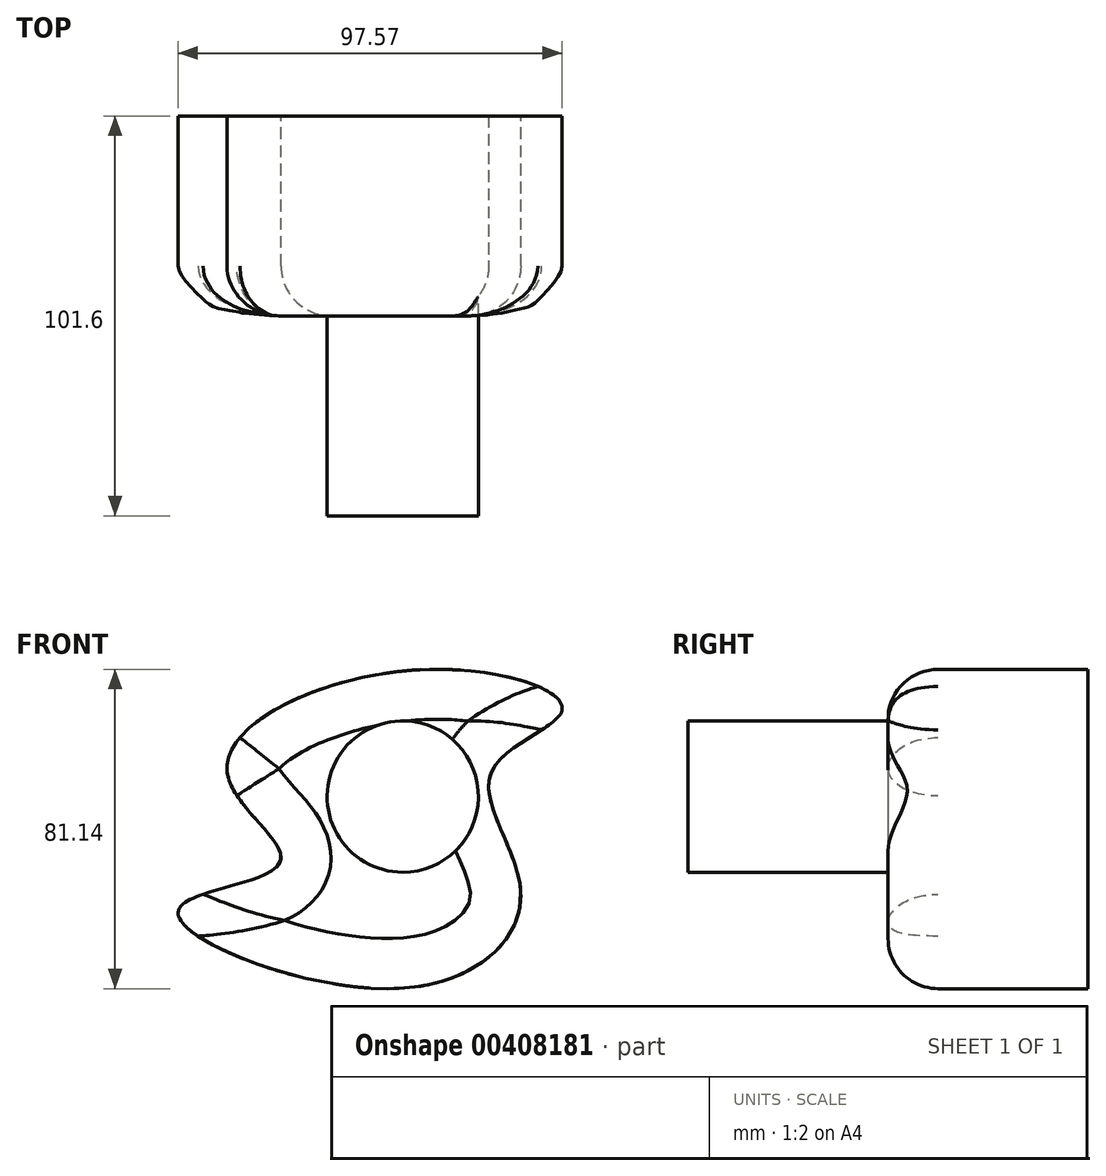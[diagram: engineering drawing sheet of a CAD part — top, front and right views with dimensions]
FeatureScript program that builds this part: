
annotation { "Feature Type Name" : "Feature", "Feature Type Description" : "" }
export const myFeature = defineFeature(function(context is Context, id is Id, definition is map)
    precondition{}
    {
        {
            var Q0;
            Q0=qCreatedBy(makeId("Front.planeOp"),FACE);
            var sketch = newSketch(context, id + "F0", { "sketchPlane" : qUnion([Q0])});
            skFitSpline(sketch, "E0", {"points": [v(39.34, -7.58) * mm, v(31.94, 23.1) * mm, v(49.8, 38.62) * mm, v(11.73, 48.9) * mm, v(-35.19, 22.74) * mm, v(-21.83, 0) * mm, v(-47.46, -11.73) * mm, v(8.3, -31.94) * mm, v(39.34, -7.58) * mm]});
            skSolve(sketch);
        }
        {
            var Q0;
            Q0 = qSketchRegion(id + "F0", true);
            extrude(context, id + "F1", {"entities" : qUnion([Q0]), "depth" : 50.8 * mm});
        }
        {
            var Q0;
            Q0=makeQuery(id+"F1.opExtrude","CAP_FACE",FACE,{"disambiguationData":[OSD([sQuery(id+"F0.wireOp",EDGE,"E0")])],"isStart":false});
            var sketch = newSketch(context, id + "F2", { "sketchPlane" : qUnion([Q0])});
            skCircle(sketch, "E1", {"center": v(9.38, 16.78) * mm, "radius": 19.23 * mm});
            skSolve(sketch);
        }
        {
            var Q0;
            Q0 = qSketchRegion(id + "F2", true);
            extrude(context, id + "F3", {"entities" : qUnion([Q0]), "operationType" : NewBodyOperationType.ADD, "depth" : 50.8 * mm});
        }
        {
            var Q0;
            Q0=makeQuery(id+"F1.opExtrude","CAP_EDGE",EDGE,{"disambiguationData":[OSD([sQuery(id+"F0.wireOp",EDGE,"E0")])],"isStart":false});
            fillet(context, id + "F4", {"entities" : qUnion([Q0]), "radius" : 12.7 * mm, "tangentPropagation" : true, "allowEdgeOverflow" : false});
        }
    });
